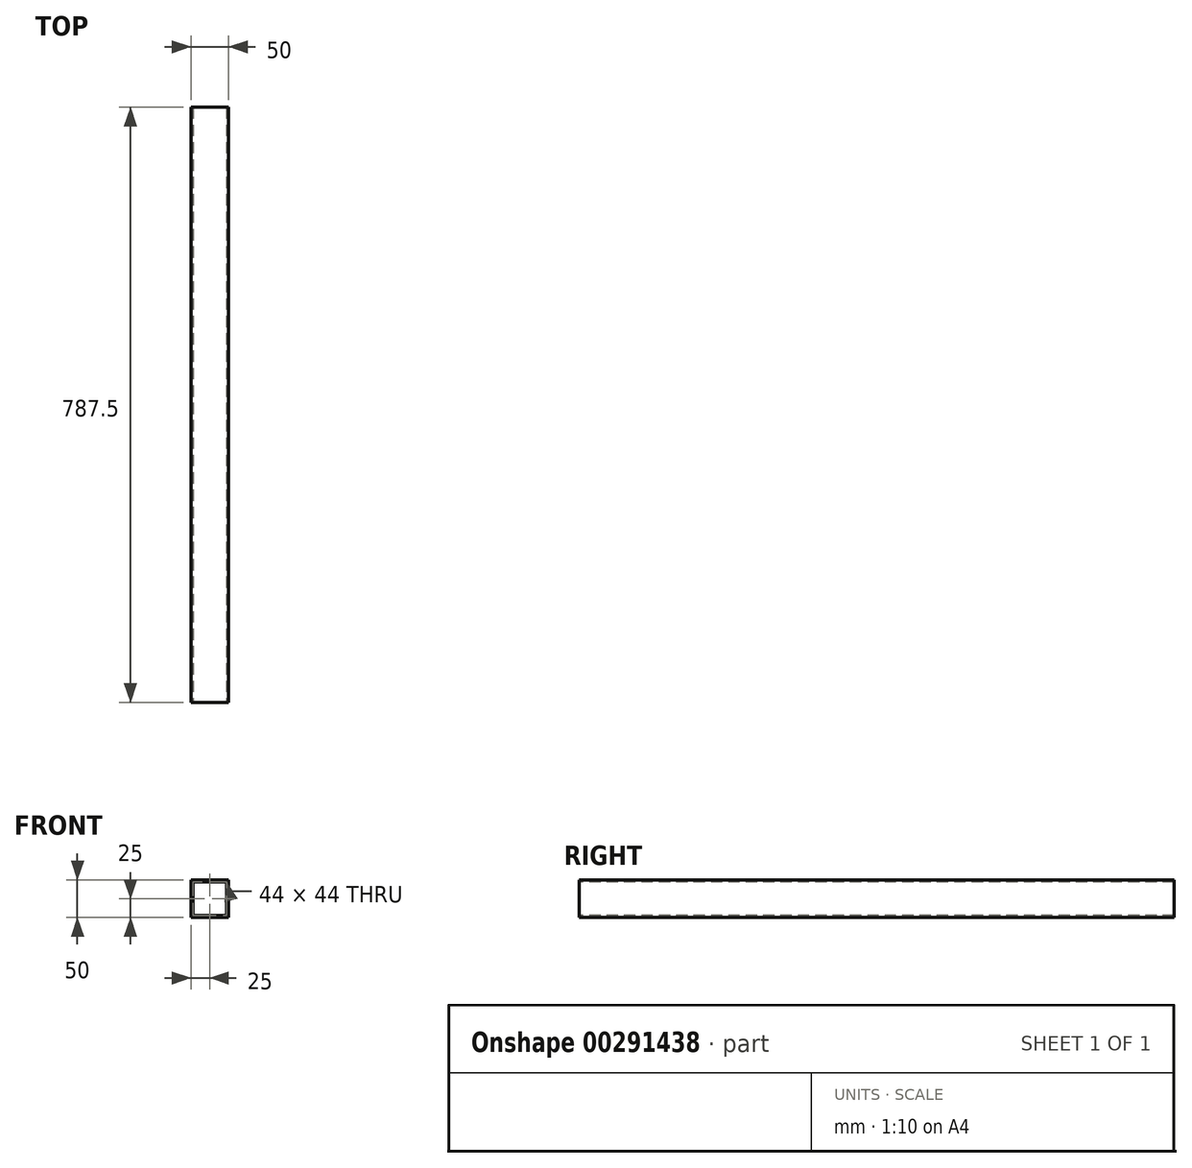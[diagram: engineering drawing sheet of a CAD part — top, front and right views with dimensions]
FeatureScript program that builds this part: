
annotation { "Feature Type Name" : "Feature", "Feature Type Description" : "" }
export const myFeature = defineFeature(function(context is Context, id is Id, definition is map)
    precondition{}
    {
        {
            var Q0;
            Q0=qCreatedBy(makeId("Front.planeOp"),FACE);
            var sketch = newSketch(context, id + "F0", { "sketchPlane" : qUnion([Q0])});
            skLineSegment(sketch, "E0.bottom", {"start": v(25, 25) * mm, "end": v(-25, 25) * mm});
            skLineSegment(sketch, "E0.top", {"start": v(25, -25) * mm, "end": v(-25, -25) * mm});
            skLineSegment(sketch, "E0.left", {"start": v(25, 25) * mm, "end": v(25, -25) * mm});
            skLineSegment(sketch, "E0.right", {"start": v(-25, 25) * mm, "end": v(-25, -25) * mm});
            skPoint(sketch, "E0.middle", {"position": v(0, 0) * mm});
            skLineSegment(sketch, "E1.0", {"start": v(22, 22) * mm, "end": v(-22, 22) * mm});
            skLineSegment(sketch, "E1.1", {"start": v(22, 22) * mm, "end": v(22, -22) * mm});
            skLineSegment(sketch, "E1.2", {"start": v(22, -22) * mm, "end": v(-22, -22) * mm});
            skLineSegment(sketch, "E1.3", {"start": v(-22, 22) * mm, "end": v(-22, -22) * mm});
            skSolve(sketch);
        }
        {
            var Q0;
            Q0=makeQuery(id+"F0.imprint","IMPRINT",FACE,{"disambiguationData":[TD([[makeQuery(id+"F0.imprint","IMPRINT",EDGE,{"derivedFrom":sQuery(id+"F0.wireOp",EDGE,"E0.bottom")}),1.0]])]});
            extrude(context, id + "F1", {"entities" : qUnion([Q0]), "oppositeDirection" : true, "depth" : 787.5 * mm});
        }
    });
